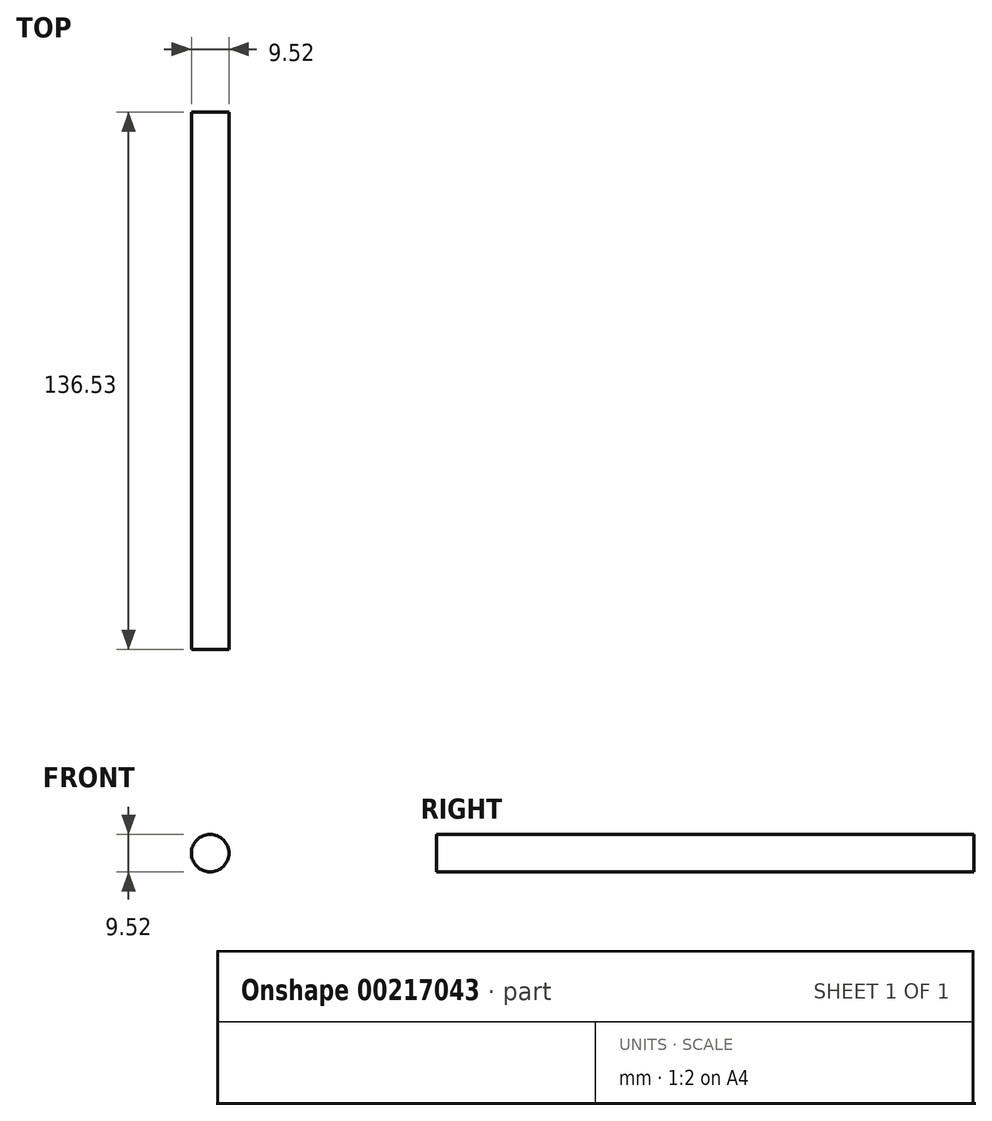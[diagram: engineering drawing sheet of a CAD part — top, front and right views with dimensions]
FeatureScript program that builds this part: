
annotation { "Feature Type Name" : "Feature", "Feature Type Description" : "" }
export const myFeature = defineFeature(function(context is Context, id is Id, definition is map)
    precondition{}
    {
        {
            var Q0;
            Q0=qCreatedBy(makeId("Front.planeOp"),FACE);
            var sketch = newSketch(context, id + "F0", { "sketchPlane" : qUnion([Q0])});
            skCircle(sketch, "E0", {"center": v(0, 0) * mm, "radius": 4.76 * mm});
            skSolve(sketch);
        }
        {
            var Q0;
            Q0=makeQuery(id+"F0.imprint","IMPRINT",FACE,{"disambiguationData":[TD([[makeQuery(id+"F0.imprint","IMPRINT",EDGE,{"derivedFrom":sQuery(id+"F0.wireOp",EDGE,"E0")}),1.0]])]});
            extrude(context, id + "F1", {"entities" : qUnion([Q0]), "depth" : 136.53 * mm});
        }
    });
